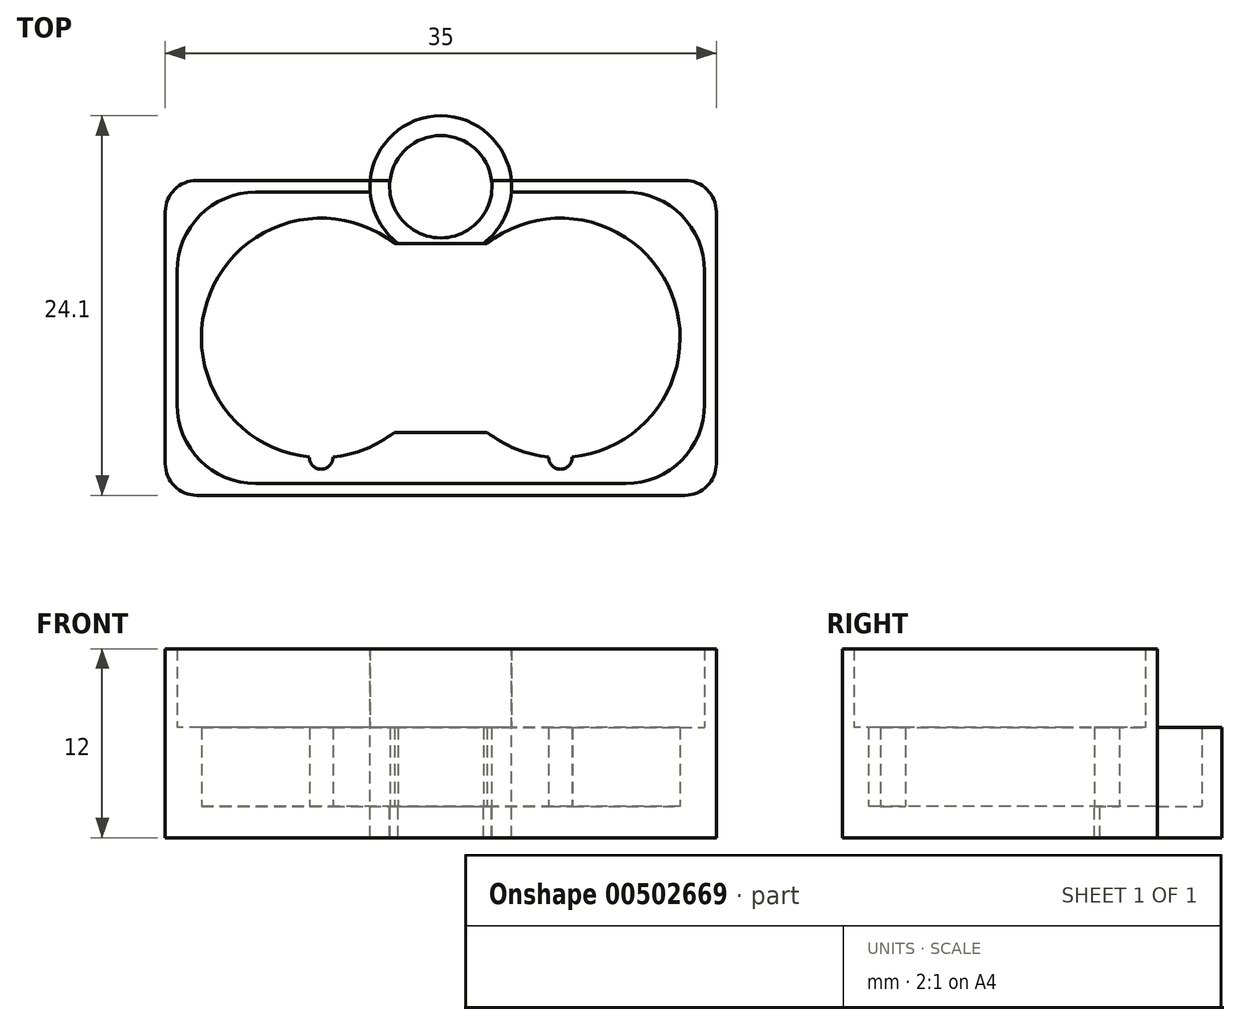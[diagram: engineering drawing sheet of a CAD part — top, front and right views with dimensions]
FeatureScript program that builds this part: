
annotation { "Feature Type Name" : "Feature", "Feature Type Description" : "" }
export const myFeature = defineFeature(function(context is Context, id is Id, definition is map)
    precondition{}
    {
        {
            var Q0;
            Q0=qCreatedBy(makeId("Top.planeOp"),FACE);
            var sketch = newSketch(context, id + "F0", { "sketchPlane" : qUnion([Q0])});
            skLineSegment(sketch, "E0", {"start": v(0, 48.4) * mm, "end": v(0, -44.37) * mm, "construction": true});
            skLineSegment(sketch, "E1", {"start": v(-7.6, 48.21) * mm, "end": v(-7.6, -44.56) * mm, "construction": true});
            skLineSegment(sketch, "E2", {"start": v(7.6, 47.25) * mm, "end": v(7.6, -45.52) * mm, "construction": true});
            skLineSegment(sketch, "E3", {"start": v(-29.15, 0) * mm, "end": v(40.62, 0) * mm, "construction": true});
            skCircle(sketch, "E4", {"center": v(-7.6, 0) * mm, "radius": 7.6 * mm});
            skCircle(sketch, "E5", {"center": v(7.6, 0) * mm, "radius": 7.6 * mm});
            skLineSegment(sketch, "E6.bottom", {"start": v(17.5, 10) * mm, "end": v(-17.5, 10) * mm});
            skLineSegment(sketch, "E6.top", {"start": v(17.5, -10) * mm, "end": v(-17.5, -10) * mm});
            skLineSegment(sketch, "E6.left", {"start": v(17.5, 10) * mm, "end": v(17.5, -10) * mm});
            skLineSegment(sketch, "E6.right", {"start": v(-17.5, 10) * mm, "end": v(-17.5, -10) * mm});
            skPoint(sketch, "E6.middle", {"position": v(0, 0) * mm});
            skLineSegment(sketch, "E7", {"start": v(-22.07, 6) * mm, "end": v(26.42, 6) * mm, "construction": true});
            skLineSegment(sketch, "E8", {"start": v(-2.94, 6) * mm, "end": v(2.94, 6) * mm});
            skLineSegment(sketch, "E9.MirrorCS", {"start": v(-29.15, 12) * mm, "end": v(40.62, 12) * mm, "construction": true});
            skLineSegment(sketch, "E10.MirrorCS", {"start": v(-2.94, -6) * mm, "end": v(2.94, -6) * mm});
            skCircle(sketch, "E11", {"center": v(0, 9.6) * mm, "radius": 3.25 * mm});
            skCircle(sketch, "E12", {"center": v(0, 9.6) * mm, "radius": 4.5 * mm});
            skCircle(sketch, "E13", {"center": v(-7.6, -7.6) * mm, "radius": 0.75 * mm});
            skCircle(sketch, "E14", {"center": v(7.6, -7.6) * mm, "radius": 0.75 * mm});
            skSolve(sketch);
        }
        {
            var Q0;
            {var subQ0=sQuery(id+"F0.wireOp",EDGE,"E12");var subQ1=sQuery(id+"F0.wireOp",EDGE,"E6.bottom");var subQ2=makeQuery(id+"F0.imprint","INTERSECT",VERTEX,{"disambiguationData":[OD(0.0)],"derivedFrom":[subQ1,subQ0]});Q0=makeQuery(id+"F0.imprint","IMPRINT",FACE,{"disambiguationData":[TD([[makeQuery(id+"F0.imprint","IMPRINT",EDGE,{"disambiguationData":[TD([[subQ2,-1.0]])],"derivedFrom":subQ1}),-1.0]])]});}
            var Q1;
            {var subQ0=sQuery(id+"F0.wireOp",EDGE,"E11");var subQ1=sQuery(id+"F0.wireOp",EDGE,"E6.bottom");var subQ2=makeQuery(id+"F0.imprint","INTERSECT",VERTEX,{"disambiguationData":[OD(0.0)],"derivedFrom":[subQ1,subQ0]});Q1=makeQuery(id+"F0.imprint","IMPRINT",FACE,{"disambiguationData":[TD([[makeQuery(id+"F0.imprint","IMPRINT",EDGE,{"disambiguationData":[TD([[subQ2,-1.0]])],"derivedFrom":subQ1}),1.0]])]});}
            var Q2;
            {var subQ0=sQuery(id+"F0.wireOp",EDGE,"E11");var subQ1=sQuery(id+"F0.wireOp",EDGE,"E6.bottom");var subQ2=makeQuery(id+"F0.imprint","INTERSECT",VERTEX,{"disambiguationData":[OD(0.0)],"derivedFrom":[subQ1,subQ0]});Q2=makeQuery(id+"F0.imprint","IMPRINT",FACE,{"disambiguationData":[TD([[makeQuery(id+"F0.imprint","IMPRINT",EDGE,{"disambiguationData":[TD([[subQ2,-1.0]])],"derivedFrom":subQ1}),-1.0]])]});}
            var Q3;
            {var subQ0=sQuery(id+"F0.wireOp",EDGE,"E8");Q3=makeQuery(id+"F0.imprint","IMPRINT",FACE,{"disambiguationData":[TD([[makeQuery(id+"F0.imprint","IMPRINT",EDGE,{"derivedFrom":subQ0}),-1.0]])]});}
            var Q4;
            {var subQ0=sQuery(id+"F0.wireOp",EDGE,"E10.MirrorCS");Q4=makeQuery(id+"F0.imprint","IMPRINT",FACE,{"disambiguationData":[TD([[makeQuery(id+"F0.imprint","IMPRINT",EDGE,{"derivedFrom":subQ0}),1.0]])]});}
            var Q5;
            {var subQ0=sQuery(id+"F0.wireOp",EDGE,"E12");var subQ1=sQuery(id+"F0.wireOp",EDGE,"E6.bottom");var subQ2=makeQuery(id+"F0.imprint","INTERSECT",VERTEX,{"disambiguationData":[OD(0.0)],"derivedFrom":[subQ1,subQ0]});Q5=makeQuery(id+"F0.imprint","IMPRINT",FACE,{"disambiguationData":[TD([[makeQuery(id+"F0.imprint","IMPRINT",EDGE,{"disambiguationData":[TD([[subQ2,-1.0]])],"derivedFrom":subQ1}),1.0]])]});}
            var Q6;
            {var subQ0=sQuery(id+"F0.wireOp",EDGE,"E4");var subQ5=makeQuery(id+"F0.imprint","INTERSECT",VERTEX,{"derivedFrom":[subQ0,sQuery(id+"F0.wireOp",EDGE,"E8")]});Q6=makeQuery(id+"F0.imprint","IMPRINT",FACE,{"disambiguationData":[TD([[makeQuery(id+"F0.imprint","IMPRINT",EDGE,{"disambiguationData":[TD([[subQ5,1.0]])],"derivedFrom":subQ0}),1.0]])]});}
            var Q7;
            {var subQ0=sQuery(id+"F0.wireOp",EDGE,"E5");var subQ1=makeQuery(id+"F0.imprint","INTERSECT",VERTEX,{"derivedFrom":[subQ0,sQuery(id+"F0.wireOp",EDGE,"E8")]});Q7=makeQuery(id+"F0.imprint","IMPRINT",FACE,{"disambiguationData":[TD([[makeQuery(id+"F0.imprint","IMPRINT",EDGE,{"disambiguationData":[TD([[subQ1,-1.0]])],"derivedFrom":subQ0}),1.0]])]});}
            var Q8;
            Q8=makeQuery(id+"F0.imprint","IMPRINT",FACE,{"disambiguationData":[TD([[makeQuery(id+"F0.imprint","IMPRINT",EDGE,{"derivedFrom":sQuery(id+"F0.wireOp",EDGE,"E6.top")}),-1.0]])]});
            var Q9;
            {var subQ0=sQuery(id+"F0.wireOp",EDGE,"E13");var subQ1=sQuery(id+"F0.wireOp",EDGE,"E4");var subQ2=makeQuery(id+"F0.imprint","INTERSECT",VERTEX,{"disambiguationData":[OD(0.0)],"derivedFrom":[subQ1,subQ0]});Q9=makeQuery(id+"F0.imprint","IMPRINT",FACE,{"disambiguationData":[TD([[makeQuery(id+"F0.imprint","IMPRINT",EDGE,{"disambiguationData":[TD([[subQ2,-1.0]])],"derivedFrom":subQ1}),1.0]])]});}
            var Q10;
            {var subQ0=sQuery(id+"F0.wireOp",EDGE,"E13");var subQ1=sQuery(id+"F0.wireOp",EDGE,"E4");var subQ2=makeQuery(id+"F0.imprint","INTERSECT",VERTEX,{"disambiguationData":[OD(0.0)],"derivedFrom":[subQ1,subQ0]});Q10=makeQuery(id+"F0.imprint","IMPRINT",FACE,{"disambiguationData":[TD([[makeQuery(id+"F0.imprint","IMPRINT",EDGE,{"disambiguationData":[TD([[subQ2,-1.0]])],"derivedFrom":subQ1}),-1.0]])]});}
            var Q11;
            {var subQ0=sQuery(id+"F0.wireOp",EDGE,"E14");var subQ1=sQuery(id+"F0.wireOp",EDGE,"E5");var subQ2=makeQuery(id+"F0.imprint","INTERSECT",VERTEX,{"disambiguationData":[OD(0.0)],"derivedFrom":[subQ1,subQ0]});Q11=makeQuery(id+"F0.imprint","IMPRINT",FACE,{"disambiguationData":[TD([[makeQuery(id+"F0.imprint","IMPRINT",EDGE,{"disambiguationData":[TD([[subQ2,-1.0]])],"derivedFrom":subQ1}),1.0]])]});}
            var Q12;
            {var subQ0=sQuery(id+"F0.wireOp",EDGE,"E14");var subQ1=sQuery(id+"F0.wireOp",EDGE,"E5");var subQ2=makeQuery(id+"F0.imprint","INTERSECT",VERTEX,{"disambiguationData":[OD(0.0)],"derivedFrom":[subQ1,subQ0]});Q12=makeQuery(id+"F0.imprint","IMPRINT",FACE,{"disambiguationData":[TD([[makeQuery(id+"F0.imprint","IMPRINT",EDGE,{"disambiguationData":[TD([[subQ2,-1.0]])],"derivedFrom":subQ1}),-1.0]])]});}
            var Q13;
            {var subQ0=sQuery(id+"F0.wireOp",EDGE,"E8");Q13=makeQuery(id+"F0.imprint","IMPRINT",FACE,{"disambiguationData":[TD([[makeQuery(id+"F0.imprint","IMPRINT",EDGE,{"derivedFrom":subQ0}),1.0]])]});}
            var Q14;
            {var subQ0=sQuery(id+"F0.wireOp",EDGE,"E12");var subQ1=sQuery(id+"F0.wireOp",EDGE,"E6.bottom");var subQ2=makeQuery(id+"F0.imprint","INTERSECT",VERTEX,{"disambiguationData":[OD(1.0)],"derivedFrom":[subQ1,subQ0]});Q14=makeQuery(id+"F0.imprint","IMPRINT",FACE,{"disambiguationData":[TD([[makeQuery(id+"F0.imprint","IMPRINT",EDGE,{"disambiguationData":[TD([[subQ2,1.0]])],"derivedFrom":subQ1}),1.0]])]});}
            var Q15;
            {var subQ0=sQuery(id+"F0.wireOp",EDGE,"lyvQzKqn-iQqp-d9GV-Jy92-Cn0W9ZC7TQAJ.top");var subQ1=sQuery(id+"F0.wireOp",EDGE,"E11");var subQ2=makeQuery(id+"F0.imprint","INTERSECT",VERTEX,{"disambiguationData":[OD(0.0)],"derivedFrom":[subQ1,subQ0]});Q15=makeQuery(id+"F0.imprint","IMPRINT",FACE,{"disambiguationData":[TD([[makeQuery(id+"F0.imprint","IMPRINT",EDGE,{"disambiguationData":[TD([[subQ2,-1.0]])],"derivedFrom":subQ1}),1.0]])]});}
            var Q16;
            {var subQ0=sQuery(id+"F0.wireOp",EDGE,"lyvQzKqn-iQqp-d9GV-Jy92-Cn0W9ZC7TQAJ.top");var subQ1=sQuery(id+"F0.wireOp",EDGE,"E11");var subQ2=makeQuery(id+"F0.imprint","INTERSECT",VERTEX,{"disambiguationData":[OD(0.0)],"derivedFrom":[subQ1,subQ0]});Q16=makeQuery(id+"F0.imprint","IMPRINT",FACE,{"disambiguationData":[TD([[makeQuery(id+"F0.imprint","IMPRINT",EDGE,{"disambiguationData":[TD([[subQ2,-1.0]])],"derivedFrom":subQ1}),-1.0]])]});}
            var Q17;
            {var subQ0=sQuery(id+"F0.wireOp",EDGE,"E12");var subQ1=sQuery(id+"F0.wireOp",EDGE,"E8");var subQ2=makeQuery(id+"F0.imprint","INTERSECT",VERTEX,{"disambiguationData":[OD(0.0)],"derivedFrom":[subQ1,subQ0]});Q17=makeQuery(id+"F0.imprint","IMPRINT",FACE,{"disambiguationData":[TD([[makeQuery(id+"F0.imprint","IMPRINT",EDGE,{"disambiguationData":[TD([[subQ2,-1.0]])],"derivedFrom":subQ1}),-1.0]])]});}
            extrude(context, id + "F1", {"entities" : qUnion([Q0, Q1, Q2, Q3, Q4, Q5, Q6, Q7, Q8, Q9, Q10, Q11, Q12, Q13, Q14, Q15, Q16, Q17]), "oppositeDirection" : true, "depth" : 2 * mm});
        }
        {
            var Q0;
            {var subQ0=sQuery(id+"F0.wireOp",EDGE,"E8");Q0=makeQuery(id+"F0.imprint","IMPRINT",FACE,{"disambiguationData":[TD([[makeQuery(id+"F0.imprint","IMPRINT",EDGE,{"derivedFrom":subQ0}),1.0]])]});}
            var Q1;
            Q1=makeQuery(id+"F0.imprint","IMPRINT",FACE,{"disambiguationData":[TD([[makeQuery(id+"F0.imprint","IMPRINT",EDGE,{"derivedFrom":sQuery(id+"F0.wireOp",EDGE,"E6.top")}),-1.0]])]});
            var Q2;
            {var subQ0=sQuery(id+"F0.wireOp",EDGE,"E12");var subQ1=sQuery(id+"F0.wireOp",EDGE,"E6.bottom");var subQ2=makeQuery(id+"F0.imprint","INTERSECT",VERTEX,{"disambiguationData":[OD(0.0)],"derivedFrom":[subQ1,subQ0]});Q2=makeQuery(id+"F0.imprint","IMPRINT",FACE,{"disambiguationData":[TD([[makeQuery(id+"F0.imprint","IMPRINT",EDGE,{"disambiguationData":[TD([[subQ2,-1.0]])],"derivedFrom":subQ1}),-1.0]])]});}
            var Q3;
            {var subQ0=sQuery(id+"F0.wireOp",EDGE,"E12");var subQ1=sQuery(id+"F0.wireOp",EDGE,"E6.bottom");var subQ2=makeQuery(id+"F0.imprint","INTERSECT",VERTEX,{"disambiguationData":[OD(1.0)],"derivedFrom":[subQ1,subQ0]});Q3=makeQuery(id+"F0.imprint","IMPRINT",FACE,{"disambiguationData":[TD([[makeQuery(id+"F0.imprint","IMPRINT",EDGE,{"disambiguationData":[TD([[subQ2,1.0]])],"derivedFrom":subQ1}),1.0]])]});}
            var Q4;
            {var subQ0=sQuery(id+"F0.wireOp",EDGE,"lyvQzKqn-iQqp-d9GV-Jy92-Cn0W9ZC7TQAJ.top");var subQ1=sQuery(id+"F0.wireOp",EDGE,"E11");var subQ2=makeQuery(id+"F0.imprint","INTERSECT",VERTEX,{"disambiguationData":[OD(0.0)],"derivedFrom":[subQ1,subQ0]});Q4=makeQuery(id+"F0.imprint","IMPRINT",FACE,{"disambiguationData":[TD([[makeQuery(id+"F0.imprint","IMPRINT",EDGE,{"disambiguationData":[TD([[subQ2,-1.0]])],"derivedFrom":subQ1}),-1.0]])]});}
            var Q5;
            {var subQ0=sQuery(id+"F0.wireOp",EDGE,"E12");var subQ1=sQuery(id+"F0.wireOp",EDGE,"E6.bottom");var subQ2=makeQuery(id+"F0.imprint","INTERSECT",VERTEX,{"disambiguationData":[OD(0.0)],"derivedFrom":[subQ1,subQ0]});Q5=makeQuery(id+"F0.imprint","IMPRINT",FACE,{"disambiguationData":[TD([[makeQuery(id+"F0.imprint","IMPRINT",EDGE,{"disambiguationData":[TD([[subQ2,-1.0]])],"derivedFrom":subQ1}),1.0]])]});}
            extrude(context, id + "F2", {"entities" : qUnion([Q0, Q1, Q2, Q3, Q4, Q5]), "operationType" : NewBodyOperationType.ADD, "depth" : 5 * mm});
        }
        {
            var Q0;
            Q0=makeQuery(id+"F2.opExtrude","CAP_FACE",FACE,{"disambiguationData":[OSD([sQuery(id+"F0.wireOp",EDGE,"E4"),sQuery(id+"F0.wireOp",EDGE,"E5"),sQuery(id+"F0.wireOp",EDGE,"E6.bottom"),sQuery(id+"F0.wireOp",EDGE,"E6.top"),sQuery(id+"F0.wireOp",EDGE,"E6.left"),sQuery(id+"F0.wireOp",EDGE,"E6.right"),sQuery(id+"F0.wireOp",EDGE,"E8"),sQuery(id+"F0.wireOp",EDGE,"E10.MirrorCS"),sQuery(id+"F0.wireOp",EDGE,"E11"),sQuery(id+"F0.wireOp",EDGE,"E12"),sQuery(id+"F0.wireOp",EDGE,"E13"),sQuery(id+"F0.wireOp",EDGE,"E14")])],"isStart":false});
            var sketch = newSketch(context, id + "F3", { "sketchPlane" : qUnion([Q0])});
            skLineSegment(sketch, "E15.bottom", {"start": v(16.75, 9.25) * mm, "end": v(-16.75, 9.25) * mm});
            skLineSegment(sketch, "E15.top", {"start": v(16.75, -9.25) * mm, "end": v(-16.75, -9.25) * mm});
            skLineSegment(sketch, "E15.left", {"start": v(16.75, 9.25) * mm, "end": v(16.75, -9.25) * mm});
            skLineSegment(sketch, "E15.right", {"start": v(-16.75, 9.25) * mm, "end": v(-16.75, -9.25) * mm});
            skPoint(sketch, "E15.middle", {"position": v(0, 0) * mm});
            skCircle(sketch, "E16", {"center": v(0, 9.6) * mm, "radius": 4 * mm});
            skSolve(sketch);
        }
        {
            var Q0;
            Q0=makeQuery(id+"F3.imprint","IMPRINT",FACE,{"disambiguationData":[TD([[makeQuery(id+"F3.imprint","IMPRINT",EDGE,{"derivedFrom":sQuery(id+"F3.wireOp",EDGE,"E15.top")}),1.0]])]});
            extrude(context, id + "F4", {"entities" : qUnion([Q0]), "operationType" : NewBodyOperationType.ADD, "depth" : 5 * mm});
        }
        {
            var Q0;
            {var subQ0=sQuery(id+"F0.wireOp",EDGE,"E6.right");var subQ1=sQuery(id+"F0.wireOp",EDGE,"E6.bottom");Q0=makeQuery(id+"F4.boolean.opBoolean","MERGE",EDGE,{"derivedFrom":[makeQuery(id+"F2.boolean.opBoolean","MERGE",EDGE,{"derivedFrom":[makeQuery(id+"F1.opExtrude","SWEPT_EDGE",EDGE,{"disambiguationData":[OSD([subQ1,subQ0])]}),makeQuery(id+"F2.opExtrude","SWEPT_EDGE",EDGE,{"disambiguationData":[OSD([subQ1,subQ0])]})]}),makeQuery(id+"F4.opExtrude","SWEPT_EDGE",EDGE,{"disambiguationData":[OSD([subQ1,subQ0])]})]});}
            var Q1;
            {var subQ0=sQuery(id+"F0.wireOp",EDGE,"E6.left");var subQ1=sQuery(id+"F0.wireOp",EDGE,"E6.bottom");Q1=makeQuery(id+"F4.boolean.opBoolean","MERGE",EDGE,{"derivedFrom":[makeQuery(id+"F2.boolean.opBoolean","MERGE",EDGE,{"derivedFrom":[makeQuery(id+"F1.opExtrude","SWEPT_EDGE",EDGE,{"disambiguationData":[OSD([subQ1,subQ0])]}),makeQuery(id+"F2.opExtrude","SWEPT_EDGE",EDGE,{"disambiguationData":[OSD([subQ1,subQ0])]})]}),makeQuery(id+"F4.opExtrude","SWEPT_EDGE",EDGE,{"disambiguationData":[OSD([subQ1,subQ0])]})]});}
            var Q2;
            {var subQ0=sQuery(id+"F0.wireOp",EDGE,"E6.left");var subQ1=sQuery(id+"F0.wireOp",EDGE,"E6.top");Q2=makeQuery(id+"F4.boolean.opBoolean","MERGE",EDGE,{"derivedFrom":[makeQuery(id+"F2.boolean.opBoolean","MERGE",EDGE,{"derivedFrom":[makeQuery(id+"F1.opExtrude","SWEPT_EDGE",EDGE,{"disambiguationData":[OSD([subQ1,subQ0])]}),makeQuery(id+"F2.opExtrude","SWEPT_EDGE",EDGE,{"disambiguationData":[OSD([subQ1,subQ0])]})]}),makeQuery(id+"F4.opExtrude","SWEPT_EDGE",EDGE,{"disambiguationData":[OSD([subQ1,subQ0])]})]});}
            var Q3;
            {var subQ0=sQuery(id+"F0.wireOp",EDGE,"E6.right");var subQ1=sQuery(id+"F0.wireOp",EDGE,"E6.top");Q3=makeQuery(id+"F4.boolean.opBoolean","MERGE",EDGE,{"derivedFrom":[makeQuery(id+"F2.boolean.opBoolean","MERGE",EDGE,{"derivedFrom":[makeQuery(id+"F1.opExtrude","SWEPT_EDGE",EDGE,{"disambiguationData":[OSD([subQ1,subQ0])]}),makeQuery(id+"F2.opExtrude","SWEPT_EDGE",EDGE,{"disambiguationData":[OSD([subQ1,subQ0])]})]}),makeQuery(id+"F4.opExtrude","SWEPT_EDGE",EDGE,{"disambiguationData":[OSD([subQ1,subQ0])]})]});}
            fillet(context, id + "F5", {"entities" : qUnion([Q0, Q1, Q2, Q3]), "radius" : 2 * mm, "tangentPropagation" : true, "allowEdgeOverflow" : false});
        }
        {
            var Q0;
            Q0=makeQuery(id+"F4.opExtrude","SWEPT_EDGE",EDGE,{"disambiguationData":[OSD([sQuery(id+"F3.wireOp",EDGE,"E15.top"),sQuery(id+"F3.wireOp",EDGE,"E15.left")])]});
            var Q1;
            Q1=makeQuery(id+"F4.opExtrude","SWEPT_EDGE",EDGE,{"disambiguationData":[OSD([sQuery(id+"F3.wireOp",EDGE,"E15.top"),sQuery(id+"F3.wireOp",EDGE,"E15.right")])]});
            var Q2;
            Q2=makeQuery(id+"F4.opExtrude","SWEPT_EDGE",EDGE,{"disambiguationData":[OSD([sQuery(id+"F3.wireOp",EDGE,"E15.bottom"),sQuery(id+"F3.wireOp",EDGE,"E15.left")])]});
            var Q3;
            Q3=makeQuery(id+"F4.opExtrude","SWEPT_EDGE",EDGE,{"disambiguationData":[OSD([sQuery(id+"F3.wireOp",EDGE,"E15.bottom"),sQuery(id+"F3.wireOp",EDGE,"E15.right")])]});
            fillet(context, id + "F6", {"entities" : qUnion([Q0, Q1, Q2, Q3]), "radius" : 5 * mm, "tangentPropagation" : true, "allowEdgeOverflow" : false});
        }
    });
